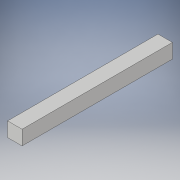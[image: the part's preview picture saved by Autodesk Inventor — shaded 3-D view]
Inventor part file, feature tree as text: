
AUTODESK INVENTOR PART (.ipt)
format: ipt  version: 2019 (Build 230136000, 136)  size: 91,648 bytes
history: native  units: in
note: dims shown in document units (in); Inventor stores cm internally (conversion verified against a paired STEP export)
features: extrude x1, sketch x1
ambient origin geometry x8: Origin, YZ Plane, XZ Plane, XY Plane, X Axis, Y Axis, Z Axis, Center Point
bodies: Solid1 (feature_tree)
feature tree (2):
  extrude  "Extrusion1"  Depth=0.125in
  sketch  "Sketch1"  dims[d0=0.125in d1=0.125in d2=1.3in d3=0.0in]
